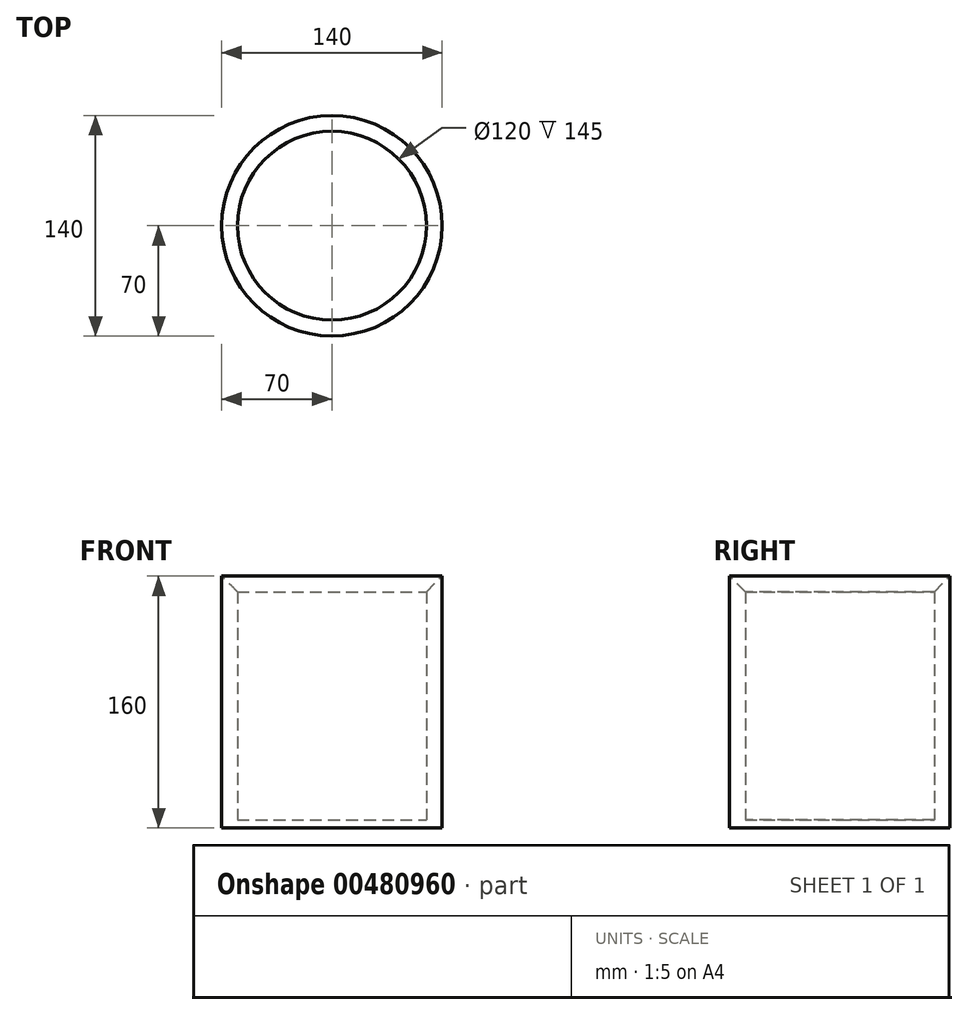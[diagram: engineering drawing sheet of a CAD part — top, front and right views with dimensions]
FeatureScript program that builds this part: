
annotation { "Feature Type Name" : "Feature", "Feature Type Description" : "" }
export const myFeature = defineFeature(function(context is Context, id is Id, definition is map)
    precondition{}
    {
        {
            var Q0;
            Q0=qCreatedBy(makeId("Front.planeOp"),FACE);
            var sketch = newSketch(context, id + "F0", { "sketchPlane" : qUnion([Q0])});
            skLineSegment(sketch, "E0", {"start": v(0, 0) * mm, "end": v(0, 5) * mm});
            skLineSegment(sketch, "E1", {"start": v(0, 5) * mm, "end": v(60, 5) * mm});
            skLineSegment(sketch, "E2", {"start": v(60, 5) * mm, "end": v(60, 150) * mm});
            skLineSegment(sketch, "E3", {"start": v(60, 150) * mm, "end": v(70, 160) * mm});
            skLineSegment(sketch, "E4", {"start": v(70, 160) * mm, "end": v(70, 0) * mm});
            skLineSegment(sketch, "E5", {"start": v(70, 0) * mm, "end": v(0, 0) * mm});
            skSolve(sketch);
        }
        {
            var Q0;
            Q0=makeQuery(id+"F0.imprint","IMPRINT",FACE,{"disambiguationData":[TD([[makeQuery(id+"F0.imprint","IMPRINT",EDGE,{"derivedFrom":sQuery(id+"F0.wireOp",EDGE,"E0")}),-1.0]])]});
            var Q1;
            Q1=sQuery(id+"F0.wireOp",EDGE,"E0");
            revolve(context, id + "F1", {"entities" : qUnion([Q0]), "axis" : qUnion([Q1]), "revolveType" : RevolveType.FULL});
        }
    });
